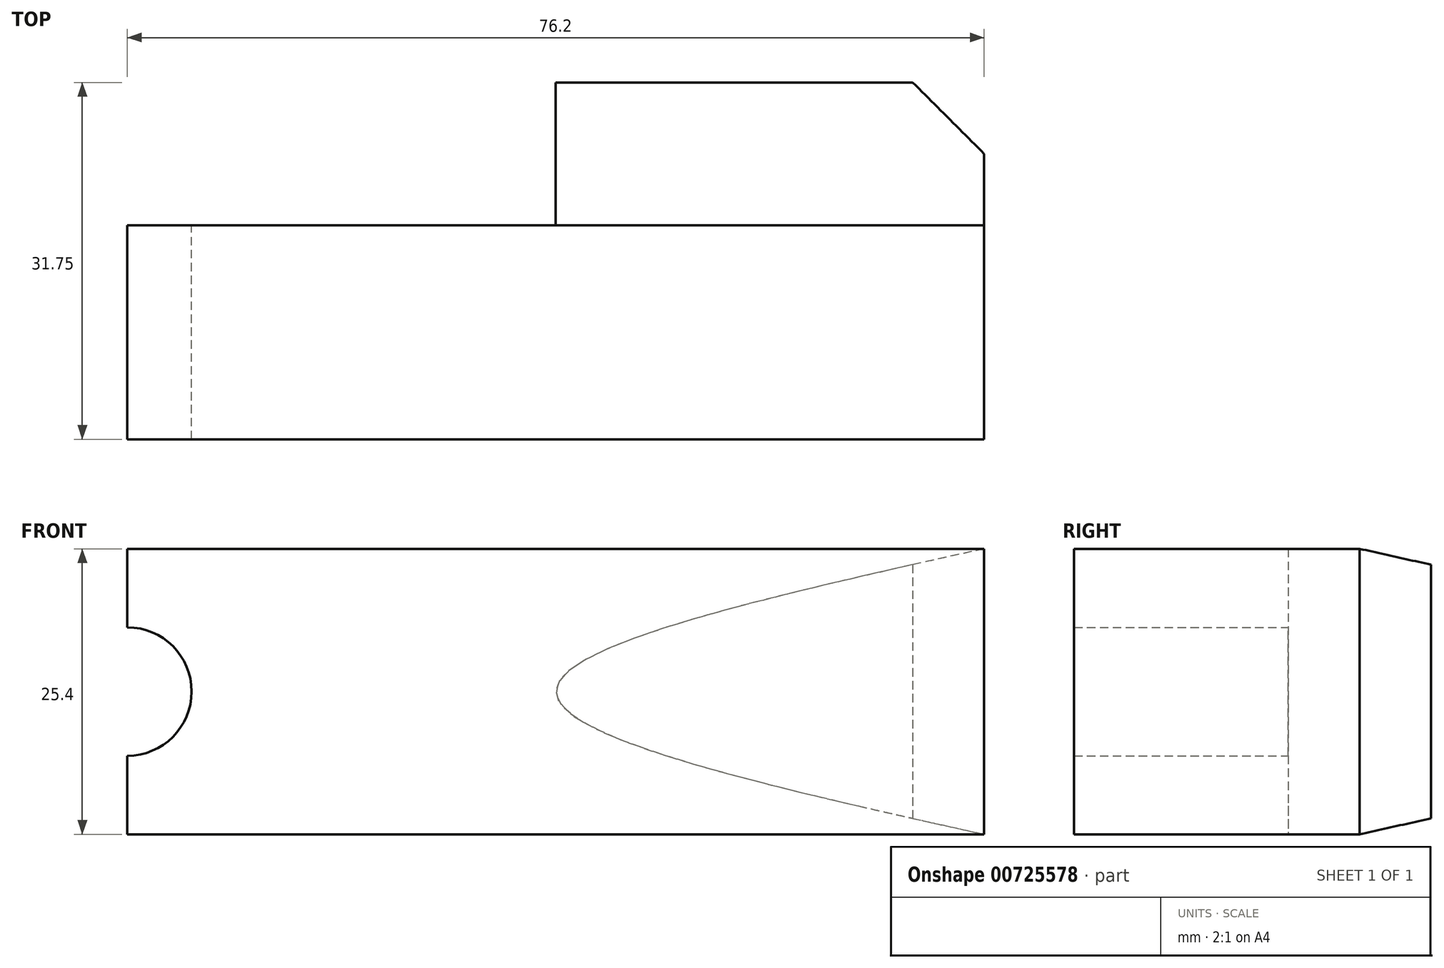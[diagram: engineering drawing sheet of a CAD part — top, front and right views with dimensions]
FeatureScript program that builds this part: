
annotation { "Feature Type Name" : "Feature", "Feature Type Description" : "" }
export const myFeature = defineFeature(function(context is Context, id is Id, definition is map)
    precondition{}
    {
        {
            var Q0;
            Q0=qCreatedBy(makeId("Front.planeOp"),FACE);
            var sketch = newSketch(context, id + "F0", { "sketchPlane" : qUnion([Q0])});
            skLineSegment(sketch, "E0.bottom", {"start": v(38.1, 12.7) * mm, "end": v(-38.1, 12.7) * mm});
            skLineSegment(sketch, "E0.top", {"start": v(38.1, -12.7) * mm, "end": v(-38.1, -12.7) * mm});
            skLineSegment(sketch, "E0.left", {"start": v(38.1, 12.7) * mm, "end": v(38.1, -12.7) * mm});
            skLineSegment(sketch, "E0.right", {"start": v(-38.1, 12.7) * mm, "end": v(-38.1, -12.7) * mm});
            skPoint(sketch, "E0.middle", {"position": v(0, 0) * mm});
            skCircle(sketch, "E1", {"center": v(-38.1, 0) * mm, "radius": 5.72 * mm});
            skSolve(sketch);
        }
        {
            var Q0;
            {var subQ1=sQuery(id+"F0.wireOp",EDGE,"E0.bottom");Q0=makeQuery(id+"F0.imprint","IMPRINT",FACE,{"disambiguationData":[TD([[makeQuery(id+"F0.imprint","IMPRINT",EDGE,{"derivedFrom":subQ1}),1.0]])]});}
            extrude(context, id + "F1", {"entities" : qUnion([Q0]), "depth" : 19.05 * mm, "offsetDistance" : 25.4 * mm});
        }
        {
            var Q0;
            Q0=makeQuery(id+"F1.opExtrude","CAP_FACE",FACE,{"disambiguationData":[OSD([sQuery(id+"F0.wireOp",EDGE,"E0.bottom"),sQuery(id+"F0.wireOp",EDGE,"E0.top"),sQuery(id+"F0.wireOp",EDGE,"E0.left"),sQuery(id+"F0.wireOp",EDGE,"E0.right"),sQuery(id+"F0.wireOp",EDGE,"E1")])],"isStart":true});
            var sketch = newSketch(context, id + "F2", { "sketchPlane" : qUnion([Q0])});
            skFitSpline(sketch, "E2", {"points": [v(-38.1, 12.7) * mm, v(0, 0) * mm, v(-38.1, -12.7) * mm], "startDerivative": vector(114.3, -25.4) * mm, "endDerivative": vector(-114.3, -25.4) * mm});
            skFitSpline(sketch, "E3", {"points": [v(-19.05, -8.47) * mm, v(-26.92, -10.18) * mm], "startDerivative": vector(-7.87, -1.7) * mm, "endDerivative": vector(-7.87, -1.7) * mm});
            skSolve(sketch);
        }
        {
            var Q0;
            {var subQ1=makeQuery(id+"F1.opExtrude","CAP_EDGE",EDGE,{"disambiguationData":[OSD([sQuery(id+"F0.wireOp",EDGE,"E0.left")])],"isStart":true});Q0=makeQuery(id+"F2.imprint","IMPRINT",FACE,{"disambiguationData":[TD([[makeQuery(id+"F2.imprint","IMPRINT",EDGE,{"derivedFrom":subQ1}),1.0]])]});}
            extrude(context, id + "F3", {"entities" : qUnion([Q0]), "operationType" : NewBodyOperationType.ADD, "depth" : 12.7 * mm, "offsetDistance" : 25.4 * mm});
        }
        {
            var Q0;
            Q0=makeQuery(id+"F3.opExtrude","CAP_EDGE",EDGE,{"disambiguationData":[OSD([sQuery(id+"F0.wireOp",EDGE,"E0.left")])],"isStart":false});
            chamfer(context, id + "F4", {"entities" : qUnion([Q0]), "width" : 6.35 * mm, "tangentPropagation" : true});
        }
    });
